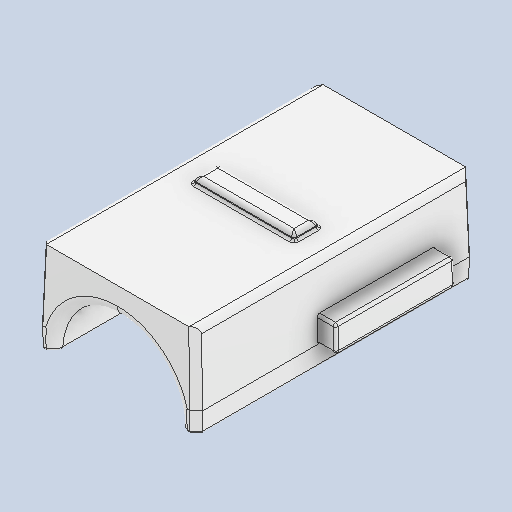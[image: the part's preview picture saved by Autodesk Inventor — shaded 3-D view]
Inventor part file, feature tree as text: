
AUTODESK INVENTOR PART (.ipt)
format: ipt  version: 2024.2 (Build 282272000, 272)  size: 407,040 bytes
history: native  units: in
note: dims shown in document units (in); Inventor stores cm internally (conversion verified against a paired STEP export)
features: fillet x1
ambient origin geometry x8: Origin, YZ Plane, XZ Plane, XY Plane, X Axis, Y Axis, Z Axis, Center Point
bodies: Solid1 (feature_tree)
feature tree (1):
  fillet  "Fillet17"  [1 undecoded]
note: 1 required parameter value undecoded (feature->parameter linkage not recoverable at this tier; creation-order binding heuristic only, values carry confidence <= 0.55)
